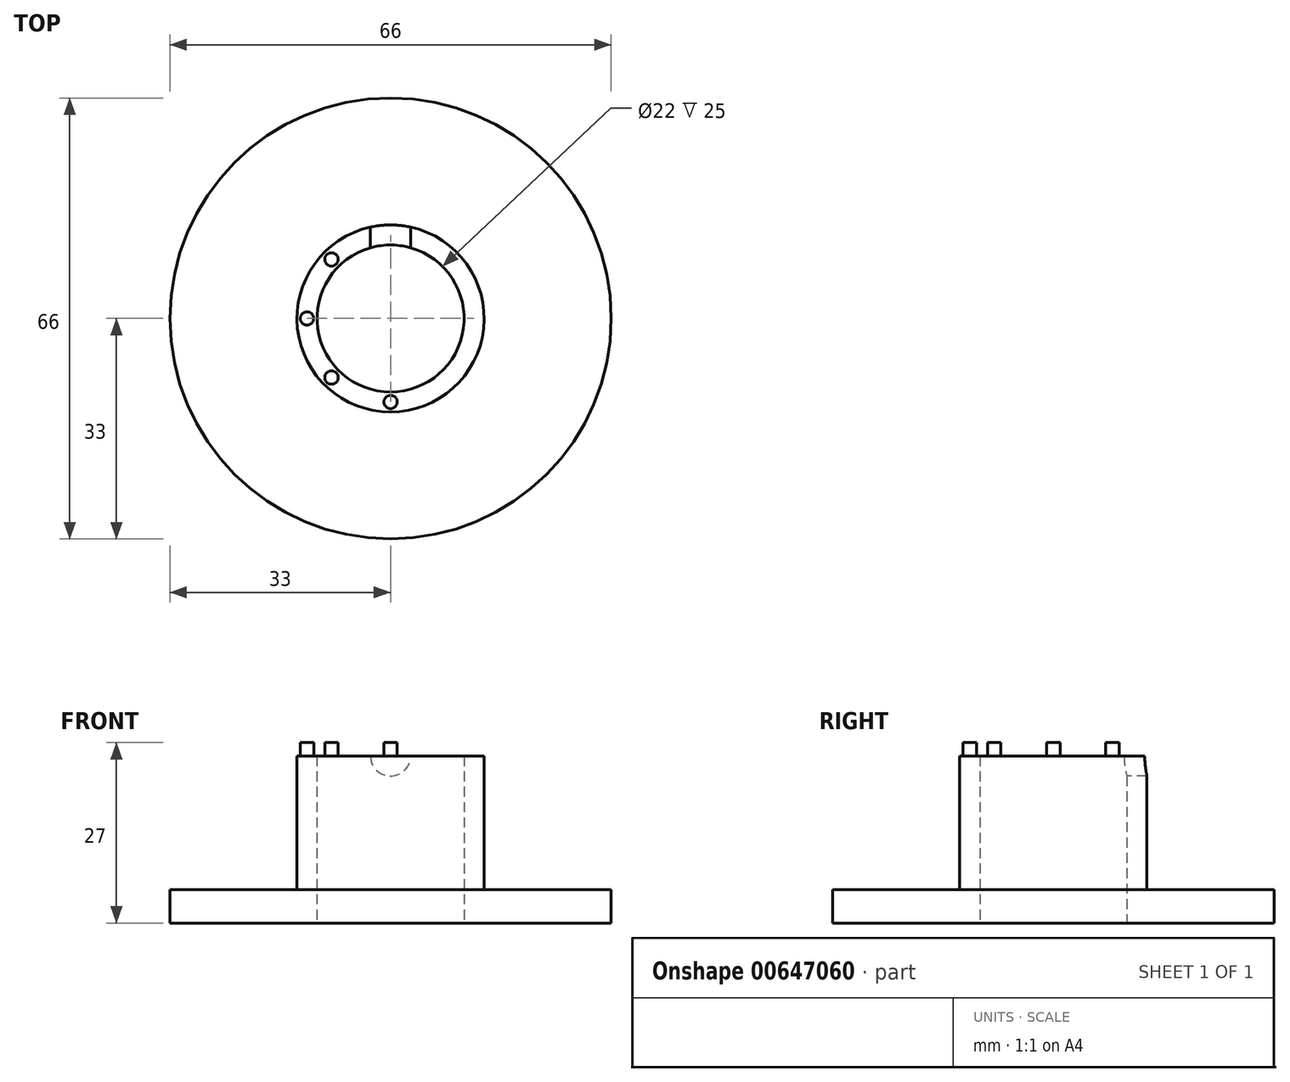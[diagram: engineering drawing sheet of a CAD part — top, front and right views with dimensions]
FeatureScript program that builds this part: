
annotation { "Feature Type Name" : "Feature", "Feature Type Description" : "" }
export const myFeature = defineFeature(function(context is Context, id is Id, definition is map)
    precondition{}
    {
        {
            var Q0;
            Q0=qCreatedBy(makeId("Top.planeOp"),FACE);
            var sketch = newSketch(context, id + "F0", { "sketchPlane" : qUnion([Q0])});
            skCircle(sketch, "E0", {"center": v(0, 0) * mm, "radius": 11 * mm});
            skCircle(sketch, "E1", {"center": v(0, 0) * mm, "radius": 33 * mm});
            skCircle(sketch, "E2.0", {"center": v(0, 0) * mm, "radius": 14 * mm});
            skSolve(sketch);
        }
        {
            var Q0;
            Q0=makeQuery(id+"F0.imprint","IMPRINT",FACE,{"disambiguationData":[TD([[makeQuery(id+"F0.imprint","IMPRINT",EDGE,{"derivedFrom":sQuery(id+"F0.wireOp",EDGE,"E0")}),-1.0]])]});
            extrude(context, id + "F1", {"entities" : qUnion([Q0]), "depth" : 25 * mm, "offsetDistance" : 25 * mm});
        }
        {
            var Q0;
            Q0=makeQuery(id+"F0.imprint","IMPRINT",FACE,{"disambiguationData":[TD([[makeQuery(id+"F0.imprint","IMPRINT",EDGE,{"derivedFrom":sQuery(id+"F0.wireOp",EDGE,"E1")}),1.0]])]});
            extrude(context, id + "F2", {"entities" : qUnion([Q0]), "operationType" : NewBodyOperationType.ADD, "depth" : 5 * mm, "offsetDistance" : 25 * mm});
        }
        {
            var Q0;
            Q0=qCreatedBy(makeId("Front.planeOp"),FACE);
            var sketch = newSketch(context, id + "F3", { "sketchPlane" : qUnion([Q0])});
            skCircle(sketch, "E3", {"center": v(0, 25) * mm, "radius": 3 * mm});
            skSolve(sketch);
        }
        {
            var Q0;
            Q0=makeQuery(id+"F3.imprint","IMPRINT",FACE,{"disambiguationData":[TD([[makeQuery(id+"F3.imprint","IMPRINT",EDGE,{"derivedFrom":sQuery(id+"F3.wireOp",EDGE,"E3")}),1.0]])]});
            extrude(context, id + "F4", {"entities" : qUnion([Q0]), "operationType" : NewBodyOperationType.REMOVE, "oppositeDirection" : true, "depth" : 25 * mm, "offsetDistance" : 25 * mm});
        }
        {
            var Q0;
            Q0=makeQuery(id+"F1.opExtrude","CAP_FACE",FACE,{"disambiguationData":[OSD([sQuery(id+"F0.wireOp",EDGE,"E0"),sQuery(id+"F0.wireOp",EDGE,"E2.0")])],"isStart":false});
            cPlane(context, id + "F5", {"entities" : qUnion([Q0]), "cplaneType" : CPlaneType.OFFSET, "offset" : 0 * mm, "width" : 150 * mm, "height" : 150 * mm});
        }
        {
            var Q0;
            Q0=qCreatedBy(id+"F5.planeOp",FACE);
            var sketch = newSketch(context, id + "F6", { "sketchPlane" : qUnion([Q0])});
            skCircle(sketch, "E4", {"center": v(0, -12.5) * mm, "radius": 1 * mm});
            skCircle(sketch, "E5.1.0", {"center": v(-8.84, -8.84) * mm, "radius": 1 * mm});
            skCircle(sketch, "E5.2.0", {"center": v(-12.5, 0) * mm, "radius": 1 * mm});
            skCircle(sketch, "E5.3.0", {"center": v(-8.84, 8.84) * mm, "radius": 1 * mm});
            skPoint(sketch, "E5.center", {"position": v(0, 0) * mm});
            skLineSegment(sketch, "E5.anchor1", {"start": v(0, 0) * mm, "end": v(0, -12.5) * mm, "construction": true});
            skLineSegment(sketch, "E5.anchor2", {"start": v(0, 0) * mm, "end": v(0, 12.5) * mm, "construction": true});
            skCircle(sketch, "E6.MirrorC", {"center": v(8.84, 8.84) * mm, "radius": 1 * mm});
            skCircle(sketch, "E7.MirrorC", {"center": v(12.5, 0) * mm, "radius": 1 * mm});
            skCircle(sketch, "E8.MirrorC", {"center": v(8.84, -8.84) * mm, "radius": 1 * mm});
            skSolve(sketch);
        }
        {
            var Q0;
            Q0=makeQuery(id+"F6.imprint","IMPRINT",FACE,{"disambiguationData":[TD([[makeQuery(id+"F6.imprint","IMPRINT",EDGE,{"derivedFrom":sQuery(id+"F6.wireOp",EDGE,"E5.3.0")}),1.0]])]});
            var Q1;
            Q1=makeQuery(id+"F6.imprint","IMPRINT",FACE,{"disambiguationData":[TD([[makeQuery(id+"F6.imprint","IMPRINT",EDGE,{"derivedFrom":sQuery(id+"F6.wireOp",EDGE,"E6.MirrorC")}),-1.0]])]});
            var Q2;
            Q2=makeQuery(id+"F6.imprint","IMPRINT",FACE,{"disambiguationData":[TD([[makeQuery(id+"F6.imprint","IMPRINT",EDGE,{"derivedFrom":sQuery(id+"F6.wireOp",EDGE,"E7.MirrorC")}),-1.0]])]});
            var Q3;
            Q3=makeQuery(id+"F6.imprint","IMPRINT",FACE,{"disambiguationData":[TD([[makeQuery(id+"F6.imprint","IMPRINT",EDGE,{"derivedFrom":sQuery(id+"F6.wireOp",EDGE,"E8.MirrorC")}),-1.0]])]});
            var Q4;
            Q4=makeQuery(id+"F6.imprint","IMPRINT",FACE,{"disambiguationData":[TD([[makeQuery(id+"F6.imprint","IMPRINT",EDGE,{"derivedFrom":sQuery(id+"F6.wireOp",EDGE,"E4")}),1.0]])]});
            var Q5;
            Q5=makeQuery(id+"F6.imprint","IMPRINT",FACE,{"disambiguationData":[TD([[makeQuery(id+"F6.imprint","IMPRINT",EDGE,{"derivedFrom":sQuery(id+"F6.wireOp",EDGE,"E5.1.0")}),1.0]])]});
            var Q6;
            Q6=makeQuery(id+"F6.imprint","IMPRINT",FACE,{"disambiguationData":[TD([[makeQuery(id+"F6.imprint","IMPRINT",EDGE,{"derivedFrom":sQuery(id+"F6.wireOp",EDGE,"E5.2.0")}),1.0]])]});
            extrude(context, id + "F7", {"entities" : qUnion([Q0, Q1, Q2, Q3, Q4, Q5, Q6]), "operationType" : NewBodyOperationType.ADD, "depth" : 2 * mm, "offsetDistance" : 25 * mm});
        }
    });
